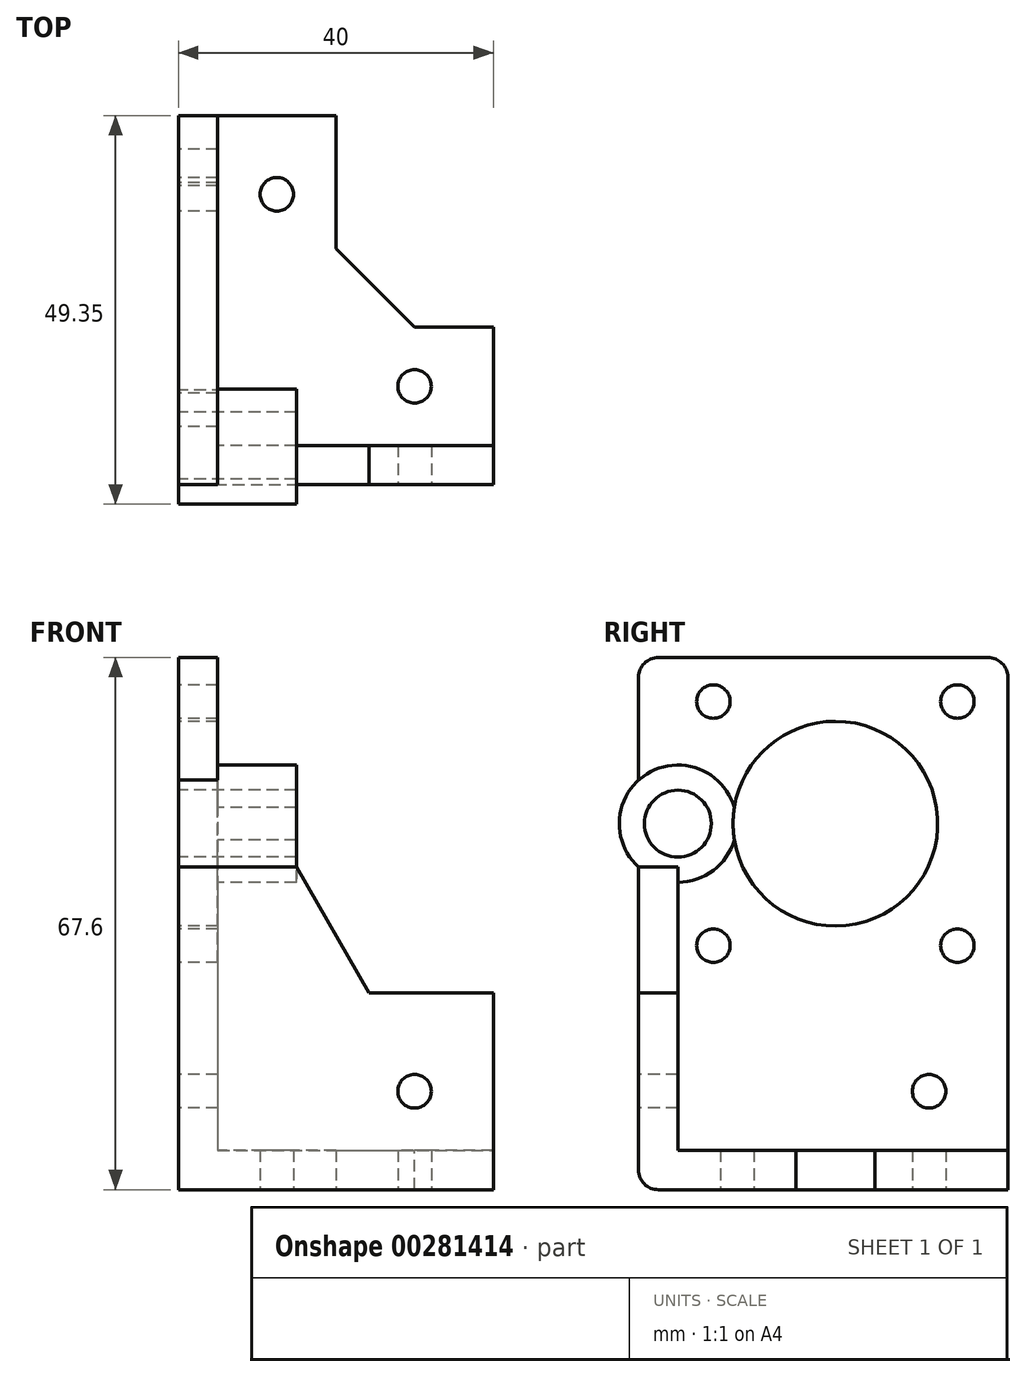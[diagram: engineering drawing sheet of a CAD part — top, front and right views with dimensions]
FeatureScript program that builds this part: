
annotation { "Feature Type Name" : "Feature", "Feature Type Description" : "" }
export const myFeature = defineFeature(function(context is Context, id is Id, definition is map)
    precondition{}
    {
        {
            var Q0;
            Q0=qCreatedBy(makeId("Top.planeOp"),FACE);
            var sketch = newSketch(context, id + "F0", { "sketchPlane" : qUnion([Q0])});
            skLineSegment(sketch, "E0", {"start": v(0, 46.9) * mm, "end": v(-20, 46.9) * mm});
            skLineSegment(sketch, "E1", {"start": v(-20, 46.9) * mm, "end": v(-20, 0) * mm});
            skLineSegment(sketch, "E2", {"start": v(-20, 0) * mm, "end": v(20, 0) * mm});
            skLineSegment(sketch, "E3", {"start": v(20, 0) * mm, "end": v(20, 20) * mm});
            skLineSegment(sketch, "E4", {"start": v(20, 20) * mm, "end": v(0, 20) * mm});
            skLineSegment(sketch, "E5", {"start": v(0, 20) * mm, "end": v(0, 46.9) * mm});
            skCircle(sketch, "E6", {"center": v(-7.5, 36.9) * mm, "radius": 2.12 * mm});
            skCircle(sketch, "E7", {"center": v(10, 12.5) * mm, "radius": 2.12 * mm});
            skCircle(sketch, "E8", {"center": v(-7.5, 12.5) * mm, "radius": 2.12 * mm, "construction": true});
            skSolve(sketch);
        }
        {
            var Q0;
            Q0=qSketchRegion(id+"F0",true);
            extrude(context, id + "F1", {"entities" : qUnion([Q0]), "depth" : 5 * mm});
        }
        {
            var Q0;
            Q0=makeQuery(id+"F1.opExtrude","CAP_FACE",FACE,{"disambiguationData":[OSD([sQuery(id+"F0.wireOp",EDGE,"E0"),sQuery(id+"F0.wireOp",EDGE,"E1"),sQuery(id+"F0.wireOp",EDGE,"E2"),sQuery(id+"F0.wireOp",EDGE,"E3"),sQuery(id+"F0.wireOp",EDGE,"E4"),sQuery(id+"F0.wireOp",EDGE,"E5"),sQuery(id+"F0.wireOp",EDGE,"E6"),sQuery(id+"F0.wireOp",EDGE,"E7")])],"isStart":false});
            var sketch = newSketch(context, id + "F2", { "sketchPlane" : qUnion([Q0])});
            skLineSegment(sketch, "E9", {"start": v(-20, 46.9) * mm, "end": v(-15, 46.9) * mm});
            skLineSegment(sketch, "E10", {"start": v(-15, 46.9) * mm, "end": v(-15, 5) * mm});
            skLineSegment(sketch, "E11", {"start": v(-15, 5) * mm, "end": v(20, 5) * mm});
            skLineSegment(sketch, "E12", {"start": v(20, 5) * mm, "end": v(20, 0) * mm});
            skLineSegment(sketch, "E13", {"start": v(20, 0) * mm, "end": v(-20, 0) * mm});
            skLineSegment(sketch, "E14", {"start": v(-20, 0) * mm, "end": v(-20, 46.9) * mm});
            skSolve(sketch);
        }
        {
            var Q0;
            Q0=qSketchRegion(id+"F2",true);
            extrude(context, id + "F3", {"entities" : qUnion([Q0]), "operationType" : NewBodyOperationType.ADD, "depth" : 20 * mm});
        }
        {
            var Q0;
            Q0=makeQuery(id+"F1.opExtrude","SWEPT_EDGE",EDGE,{"disambiguationData":[OSD([sQuery(id+"F0.wireOp",EDGE,"E4"),sQuery(id+"F0.wireOp",EDGE,"E5")])]});
            var Q1;
            Q1=makeQuery(id+"F76PTgu7nN6sp4q_1.opExtrude","CAP_EDGE",EDGE,{"disambiguationData":[OSD([sQuery(id+"FVZp2BhR3DRSIo4_1.wireOp",EDGE,"NxikKBTB-JvOB-kXal-Y067-Dro2nPYKC55K")])],"isStart":true});
            var Q2;
            Q2=makeQuery(id+"F76PTgu7nN6sp4q_1.opExtrude","CAP_EDGE",EDGE,{"disambiguationData":[OSD([sQuery(id+"FVZp2BhR3DRSIo4_1.wireOp",EDGE,"2QbokhEA-Neii-4Odm-KCon-wAkmbLHXTRdn")])],"isStart":true});
            chamfer(context, id + "F4", {"entities" : qUnion([Q0, Q1, Q2]), "width" : 10 * mm, "tangentPropagation" : true});
        }
        {
            var Q0;
            Q0=makeQuery(id+"F76PTgu7nN6sp4q_1.boolean.opBoolean","MERGE",FACE,{"derivedFrom":[makeQuery(id+"F3.boolean.opBoolean","MERGE",FACE,{"derivedFrom":[makeQuery(id+"F1.opExtrude","SWEPT_FACE",FACE,{"disambiguationData":[OSD([sQuery(id+"F0.wireOp",EDGE,"E2")])]}),makeQuery(id+"F3.opExtrude","SWEPT_FACE",FACE,{"disambiguationData":[OSD([sQuery(id+"F2.wireOp",EDGE,"E13")])]})]}),makeQuery(id+"F76PTgu7nN6sp4q_1.opExtrude","SWEPT_FACE",FACE,{"disambiguationData":[OSD([sQuery(id+"FVZp2BhR3DRSIo4_1.wireOp",EDGE,"PXxosK55-A00r-EiAo-lVqn-v3T7ZulwWpec")])]})]});
            var sketch = newSketch(context, id + "F5", { "sketchPlane" : qUnion([Q0])});
            skCircle(sketch, "E15", {"center": v(10, 12.5) * mm, "radius": 2.12 * mm});
            skSolve(sketch);
        }
        {
            var Q0;
            Q0=qSketchRegion(id+"F5",true);
            extrude(context, id + "F6", {"entities" : qUnion([Q0]), "operationType" : NewBodyOperationType.REMOVE, "oppositeDirection" : true, "depth" : 5 * mm});
        }
        {
            var Q0;
            Q0=makeQuery(id+"F76PTgu7nN6sp4q_1.boolean.opBoolean","MERGE",FACE,{"derivedFrom":[makeQuery(id+"F3.boolean.opBoolean","MERGE",FACE,{"derivedFrom":[makeQuery(id+"F1.opExtrude","SWEPT_FACE",FACE,{"disambiguationData":[OSD([sQuery(id+"F0.wireOp",EDGE,"E1")])]}),makeQuery(id+"F3.opExtrude","SWEPT_FACE",FACE,{"disambiguationData":[OSD([sQuery(id+"F2.wireOp",EDGE,"E14")])]})]}),makeQuery(id+"F76PTgu7nN6sp4q_1.opExtrude","SWEPT_FACE",FACE,{"disambiguationData":[OSD([sQuery(id+"FVZp2BhR3DRSIo4_1.wireOp",EDGE,"IHTPssIf-bVww-9Vql-ndyx-yP6tfeN2iFFo")])]})]});
            var sketch = newSketch(context, id + "F7", { "sketchPlane" : qUnion([Q0])});
            skCircle(sketch, "E16", {"center": v(-36.9, 12.5) * mm, "radius": 2.12 * mm});
            skSolve(sketch);
        }
        {
            var Q0;
            Q0=qSketchRegion(id+"F7",true);
            extrude(context, id + "F8", {"entities" : qUnion([Q0]), "operationType" : NewBodyOperationType.REMOVE, "oppositeDirection" : true, "depth" : 5 * mm});
        }
        {
            var Q0;
            Q0=makeQuery(id+"F3.opExtrude","CAP_FACE",FACE,{"disambiguationData":[OSD([sQuery(id+"F2.wireOp",EDGE,"E9"),sQuery(id+"F2.wireOp",EDGE,"E10"),sQuery(id+"F2.wireOp",EDGE,"E11"),sQuery(id+"F2.wireOp",EDGE,"E12"),sQuery(id+"F2.wireOp",EDGE,"E13"),sQuery(id+"F2.wireOp",EDGE,"E14")])],"isStart":false});
            var sketch = newSketch(context, id + "F9", { "sketchPlane" : qUnion([Q0])});
            skPoint(sketch, "E17.oppositeSnap0", {"position": v(-15, 25.95) * mm});
            skLineSegment(sketch, "E17.bottom", {"start": v(-20, 46.9) * mm, "end": v(-15, 46.9) * mm});
            skLineSegment(sketch, "E17.top", {"start": v(-20, 0) * mm, "end": v(-15, 0) * mm});
            skLineSegment(sketch, "E17.left", {"start": v(-20, 46.9) * mm, "end": v(-20, 0) * mm});
            skLineSegment(sketch, "E17.right", {"start": v(-15, 46.9) * mm, "end": v(-15, 0) * mm});
            skSolve(sketch);
        }
        {
            var Q0;
            Q0=qSketchRegion(id+"F9",true);
            extrude(context, id + "F10", {"entities" : qUnion([Q0]), "operationType" : NewBodyOperationType.ADD, "depth" : 42.6 * mm});
        }
        {
            var Q0;
            Q0=makeQuery(id+"F10.boolean.opBoolean","MERGE",FACE,{"derivedFrom":[makeQuery(id+"F3.boolean.opBoolean","MERGE",FACE,{"derivedFrom":[makeQuery(id+"F1.opExtrude","SWEPT_FACE",FACE,{"disambiguationData":[OSD([sQuery(id+"F0.wireOp",EDGE,"E1")])]}),makeQuery(id+"F3.opExtrude","SWEPT_FACE",FACE,{"disambiguationData":[OSD([sQuery(id+"F2.wireOp",EDGE,"E14")])]})]}),makeQuery(id+"F10.opExtrude","SWEPT_FACE",FACE,{"disambiguationData":[OSD([sQuery(id+"F9.wireOp",EDGE,"E17.left")])]})]});
            var sketch = newSketch(context, id + "F11", { "sketchPlane" : qUnion([Q0])});
            skLineSegment(sketch, "E18.bottom", {"start": v(-9.5, 31) * mm, "end": v(-40.5, 31) * mm, "construction": true});
            skLineSegment(sketch, "E18.top", {"start": v(-9.5, 62) * mm, "end": v(-40.5, 62) * mm, "construction": true});
            skLineSegment(sketch, "E18.left", {"start": v(-9.5, 31) * mm, "end": v(-9.5, 62) * mm, "construction": true});
            skLineSegment(sketch, "E18.right", {"start": v(-40.5, 31) * mm, "end": v(-40.5, 62) * mm, "construction": true});
            skPoint(sketch, "E18.middle", {"position": v(-25, 46.5) * mm});
            skCircle(sketch, "E19", {"center": v(-40.5, 62) * mm, "radius": 2.12 * mm});
            skCircle(sketch, "E20", {"center": v(-9.5, 62) * mm, "radius": 2.12 * mm});
            skCircle(sketch, "E21", {"center": v(-9.5, 31) * mm, "radius": 2.12 * mm});
            skCircle(sketch, "E22", {"center": v(-40.5, 31) * mm, "radius": 2.12 * mm});
            skCircle(sketch, "E23", {"center": v(-25, 46.5) * mm, "radius": 13 * mm});
            skCircle(sketch, "E24", {"center": v(-5, 46.5) * mm, "radius": 4.25 * mm});
            skSolve(sketch);
        }
        {
            var Q0;
            Q0=qSketchRegion(id+"F11",true);
            extrude(context, id + "F12", {"entities" : qUnion([Q0]), "operationType" : NewBodyOperationType.REMOVE, "endBound" : BoundingType.THROUGH_ALL, "oppositeDirection" : true, "depth" : 25 * mm});
        }
        {
            var Q0;
            Q0=makeQuery(id+"F10.opExtrude","CAP_EDGE",EDGE,{"disambiguationData":[OSD([sQuery(id+"F9.wireOp",EDGE,"E17.top")])],"isStart":false});
            var Q1;
            Q1=makeQuery(id+"F10.opExtrude","CAP_EDGE",EDGE,{"disambiguationData":[OSD([sQuery(id+"F9.wireOp",EDGE,"E17.bottom")])],"isStart":false});
            var Q2;
            Q2=makeQuery(id+"F1.opExtrude","CAP_EDGE",EDGE,{"disambiguationData":[OSD([sQuery(id+"F0.wireOp",EDGE,"E2")])],"isStart":true});
            fillet(context, id + "F13", {"entities" : qUnion([Q0, Q1, Q2]), "radius" : 2.5 * mm, "tangentPropagation" : true, "allowEdgeOverflow" : false});
        }
        {
            var Q0;
            Q0=makeQuery(id+"F10.boolean.opBoolean","MERGE",FACE,{"derivedFrom":[makeQuery(id+"F3.opExtrude","SWEPT_FACE",FACE,{"disambiguationData":[OSD([sQuery(id+"F2.wireOp",EDGE,"E10")])]}),makeQuery(id+"F10.opExtrude","SWEPT_FACE",FACE,{"disambiguationData":[OSD([sQuery(id+"F9.wireOp",EDGE,"E17.right")])]})]});
            var sketch = newSketch(context, id + "F14", { "sketchPlane" : qUnion([Q0])});
            skCircle(sketch, "E25", {"center": v(5, 46.5) * mm, "radius": 4.25 * mm});
            skArc(sketch, "E26", {"start": v(12.16, 48.55) * mm, "mid": v(7.05, 53.66) * mm, "end": v(0, 52.02) * mm});
            skArc(sketch, "E27", {"start": v(12.16, 48.55) * mm, "mid": v(12, 46.5) * mm, "end": v(12.16, 44.45) * mm});
            skLineSegment(sketch, "E28", {"start": v(0, 52.02) * mm, "end": v(0, 40.98) * mm});
            skArc(sketch, "E29.trimOffspring", {"start": v(0, 40.98) * mm, "mid": v(7.05, 39.34) * mm, "end": v(12.16, 44.45) * mm});
            skSolve(sketch);
        }
        {
            var Q0;
            Q0=qSketchRegion(id+"F14",true);
            extrude(context, id + "F15", {"entities" : qUnion([Q0]), "operationType" : NewBodyOperationType.ADD, "depth" : 10 * mm});
        }
        {
            var Q0;
            Q0=makeQuery(id+"F15.boolean.opBoolean","MERGE",FACE,{"derivedFrom":[makeQuery(id+"F10.boolean.opBoolean","MERGE",FACE,{"derivedFrom":[makeQuery(id+"F3.boolean.opBoolean","MERGE",FACE,{"derivedFrom":[makeQuery(id+"F1.opExtrude","SWEPT_FACE",FACE,{"disambiguationData":[OSD([sQuery(id+"F0.wireOp",EDGE,"E2")])]}),makeQuery(id+"F3.opExtrude","SWEPT_FACE",FACE,{"disambiguationData":[OSD([sQuery(id+"F2.wireOp",EDGE,"E13")])]})]}),makeQuery(id+"F10.opExtrude","SWEPT_FACE",FACE,{"disambiguationData":[OSD([sQuery(id+"F9.wireOp",EDGE,"E17.top")])]})]}),makeQuery(id+"F15.opExtrude","SWEPT_FACE",FACE,{"disambiguationData":[OSD([sQuery(id+"F14.wireOp",EDGE,"E28")])]})]});
            var sketch = newSketch(context, id + "F16", { "sketchPlane" : qUnion([Q0])});
            skLineSegment(sketch, "E30", {"start": v(-5, 40.98) * mm, "end": v(-15, 40.98) * mm});
            skLineSegment(sketch, "E31", {"start": v(-15, 40.98) * mm, "end": v(-15, 25) * mm});
            skLineSegment(sketch, "E32", {"start": v(-15, 25) * mm, "end": v(4.22, 25) * mm});
            skLineSegment(sketch, "E33", {"start": v(4.22, 25) * mm, "end": v(-5, 40.98) * mm});
            skSolve(sketch);
        }
        {
            var Q0;
            Q0=qSketchRegion(id+"F16",true);
            extrude(context, id + "F17", {"entities" : qUnion([Q0]), "operationType" : NewBodyOperationType.ADD, "oppositeDirection" : true, "depth" : 5 * mm});
        }
        {
            var Q0;
            Q0=makeQuery(id+"FFKOx9rv4dInz5n_1.opChamfer","SPLIT",FACE,{"disambiguationData":[OD(0.0)],"derivedFrom":makeQuery(id+"F10.boolean.opBoolean","MERGE",FACE,{"derivedFrom":[makeQuery(id+"F3.opExtrude","SWEPT_FACE",FACE,{"disambiguationData":[OSD([sQuery(id+"F2.wireOp",EDGE,"E10")])]}),makeQuery(id+"F10.opExtrude","SWEPT_FACE",FACE,{"disambiguationData":[OSD([sQuery(id+"F9.wireOp",EDGE,"E17.right")])]})]})});
            var sketch = newSketch(context, id + "F18", { "sketchPlane" : qUnion([Q0])});
            skCircle(sketch, "E34", {"center": v(9.5, 31) * mm, "radius": 3.5 * mm});
            skSolve(sketch);
        }
        {
            var Q0;
            Q0=qSketchRegion(id+"F18",true);
            extrude(context, id + "F19", {"entities" : qUnion([Q0]), "operationType" : NewBodyOperationType.REMOVE, "depth" : 25 * mm});
        }
        {
            var Q0;
            Q0=makeQuery(id+"F15.opExtrude","CAP_FACE",FACE,{"disambiguationData":[OSD([sQuery(id+"F14.wireOp",EDGE,"E25"),sQuery(id+"F14.wireOp",EDGE,"E26"),sQuery(id+"F14.wireOp",EDGE,"E27"),sQuery(id+"F14.wireOp",EDGE,"E28"),sQuery(id+"F14.wireOp",EDGE,"E29.trimOffspring")])],"isStart":false});
            var sketch = newSketch(context, id + "F20", { "sketchPlane" : qUnion([Q0])});
            skCircle(sketch, "E35", {"center": v(5, 46.5) * mm, "radius": 4.25 * mm});
            skArc(sketch, "E36", {"start": v(12.16, 48.55) * mm, "mid": v(-2.45, 46.5) * mm, "end": v(12.16, 44.45) * mm});
            skArc(sketch, "E37", {"start": v(12.16, 48.55) * mm, "mid": v(12, 46.5) * mm, "end": v(12.16, 44.45) * mm});
            skSolve(sketch);
        }
        {
            var Q0;
            Q0=qSketchRegion(id+"F20",true);
            extrude(context, id + "F21", {"entities" : qUnion([Q0]), "operationType" : NewBodyOperationType.ADD, "oppositeDirection" : true, "depth" : 15 * mm});
        }
    });
